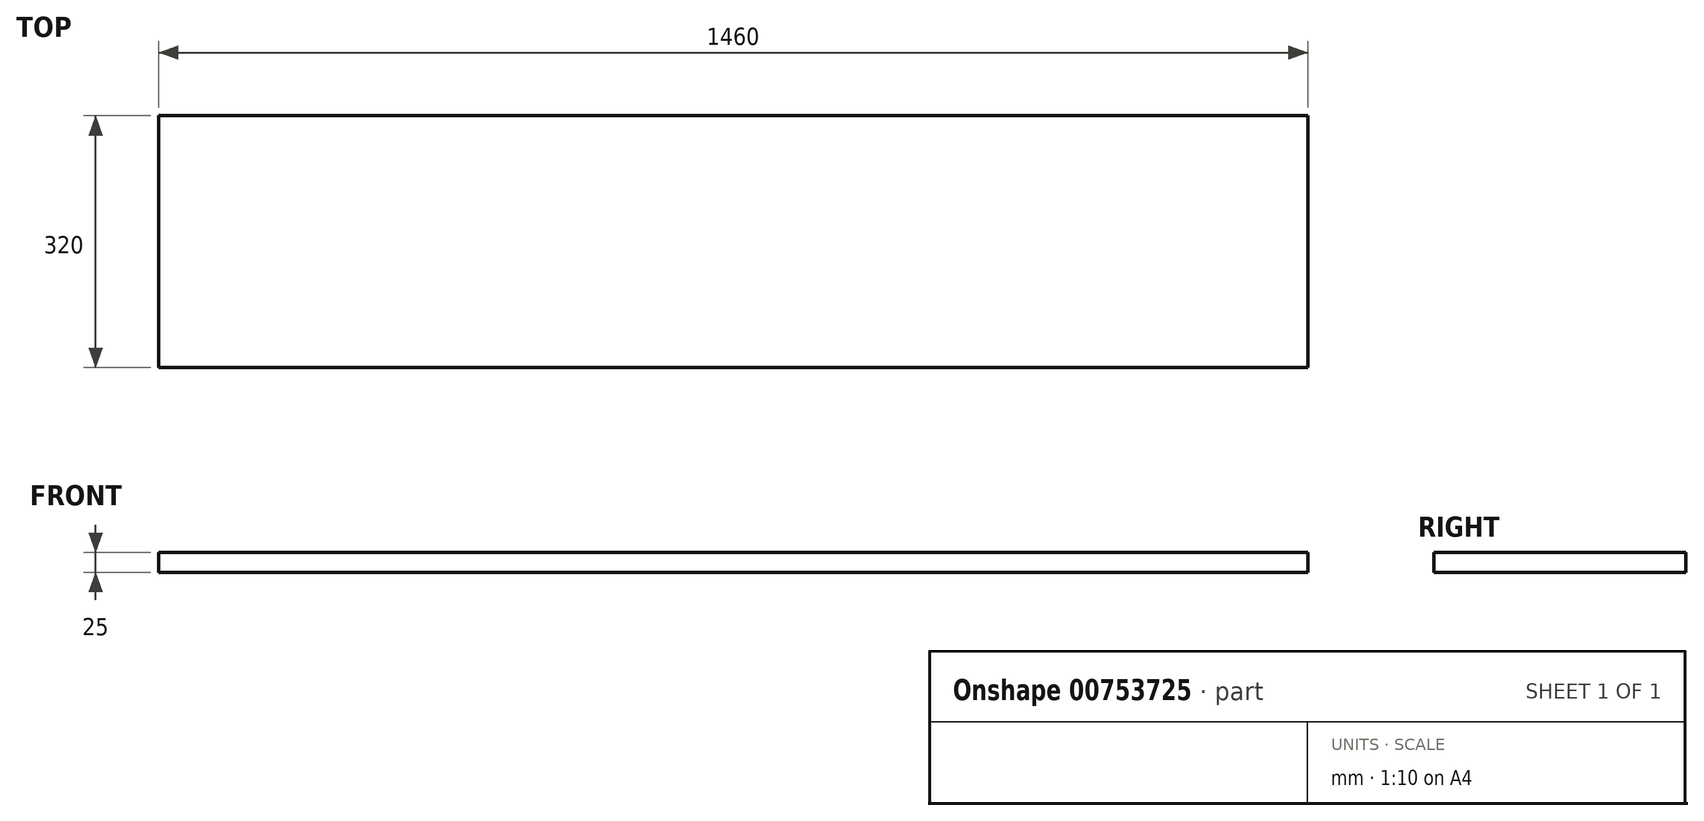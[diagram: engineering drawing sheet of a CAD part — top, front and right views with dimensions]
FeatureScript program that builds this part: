
annotation { "Feature Type Name" : "Feature", "Feature Type Description" : "" }
export const myFeature = defineFeature(function(context is Context, id is Id, definition is map)
    precondition{}
    {
        {
            var Q0;
            Q0=qCreatedBy(makeId("Top.planeOp"),FACE);
            var sketch = newSketch(context, id + "F0", { "sketchPlane" : qUnion([Q0])});
            skLineSegment(sketch, "E0.bottom", {"start": v(730, -160) * mm, "end": v(-730, -160) * mm});
            skLineSegment(sketch, "E0.top", {"start": v(730, 160) * mm, "end": v(-730, 160) * mm});
            skLineSegment(sketch, "E0.left", {"start": v(730, -160) * mm, "end": v(730, 160) * mm});
            skLineSegment(sketch, "E0.right", {"start": v(-730, -160) * mm, "end": v(-730, 160) * mm});
            skPoint(sketch, "E0.middle", {"position": v(0, 0) * mm});
            skSolve(sketch);
        }
        {
            var Q0;
            Q0=makeQuery(id+"F0.imprint","IMPRINT",FACE,{"disambiguationData":[TD([[makeQuery(id+"F0.imprint","IMPRINT",EDGE,{"derivedFrom":sQuery(id+"F0.wireOp",EDGE,"E0.bottom")}),-1.0]])]});
            extrude(context, id + "F1", {"entities" : qUnion([Q0]), "depth" : 25 * mm, "offsetDistance" : 25 * mm});
        }
    });
